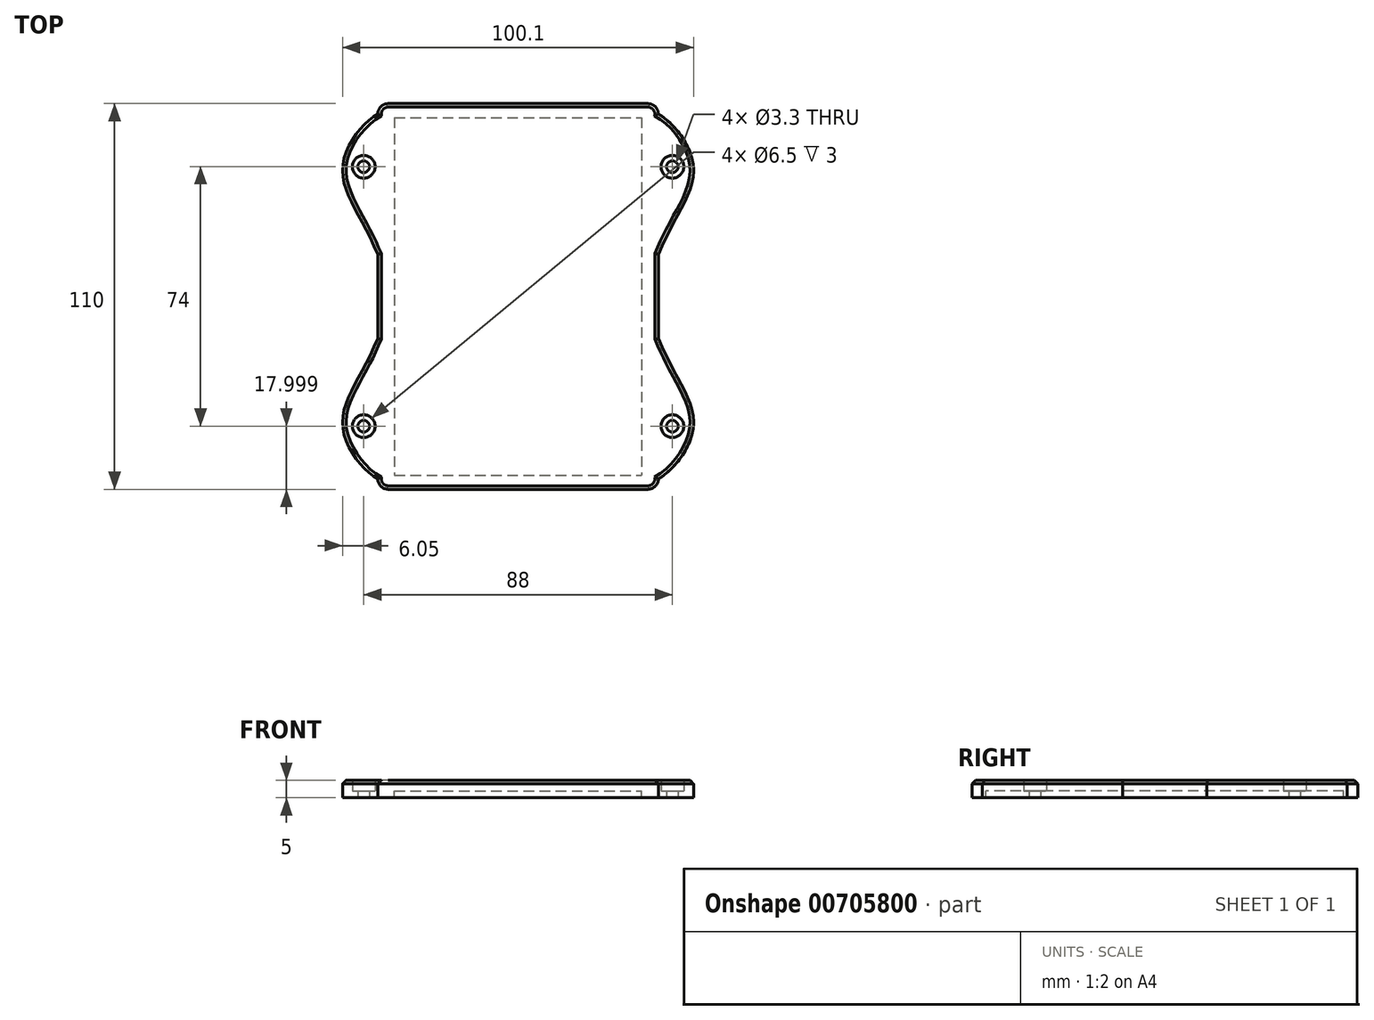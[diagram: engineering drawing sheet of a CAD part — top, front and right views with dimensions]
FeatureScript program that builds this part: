
annotation { "Feature Type Name" : "Feature", "Feature Type Description" : "" }
export const myFeature = defineFeature(function(context is Context, id is Id, definition is map)
    precondition{}
    {
        {
            var Q0;
            Q0=qCreatedBy(makeId("Top.planeOp"),FACE);
            var sketch = newSketch(context, id + "F0", { "sketchPlane" : qUnion([Q0])});
            skLineSegment(sketch, "E0.bottom", {"start": v(-37, 55.33) * mm, "end": v(37, 55.33) * mm});
            skLineSegment(sketch, "E0.top", {"start": v(-37, -54.67) * mm, "end": v(37, -54.67) * mm});
            skLineSegment(sketch, "E0.left", {"start": v(-40, 52.33) * mm, "end": v(-40, -51.67) * mm});
            skLineSegment(sketch, "E0.right", {"start": v(40, 52.33) * mm, "end": v(40, -51.67) * mm});
            skPoint(sketch, "E1.visualSharp", {"position": v(-40, 55.33) * mm});
            skArc(sketch, "E1.filletArc", {"start": v(-37, 55.33) * mm, "mid": v(-39.12, 54.45) * mm, "end": v(-40, 52.33) * mm});
            skPoint(sketch, "E2.visualSharp", {"position": v(40, 55.33) * mm});
            skArc(sketch, "E2.filletArc", {"start": v(40, 52.33) * mm, "mid": v(39.12, 54.45) * mm, "end": v(37, 55.33) * mm});
            skPoint(sketch, "E3.visualSharp", {"position": v(-40, -54.67) * mm});
            skArc(sketch, "E3.filletArc", {"start": v(-40, -51.67) * mm, "mid": v(-39.12, -53.8) * mm, "end": v(-37, -54.67) * mm});
            skPoint(sketch, "E4.visualSharp", {"position": v(40, -54.67) * mm});
            skArc(sketch, "E4.filletArc", {"start": v(37, -54.67) * mm, "mid": v(39.12, -53.8) * mm, "end": v(40, -51.67) * mm});
            skLineSegment(sketch, "E5.bottom", {"start": v(-35.25, 51.33) * mm, "end": v(35.25, 51.33) * mm});
            skLineSegment(sketch, "E5.top", {"start": v(-35.25, -50.67) * mm, "end": v(35.25, -50.67) * mm});
            skLineSegment(sketch, "E5.left", {"start": v(-35.25, 51.33) * mm, "end": v(-35.25, -50.67) * mm});
            skLineSegment(sketch, "E5.right", {"start": v(35.25, 51.33) * mm, "end": v(35.25, -50.67) * mm});
            skPoint(sketch, "E6", {"position": v(-30.86, 36.33) * mm});
            skPoint(sketch, "E7.MirrorP", {"position": v(30.86, 36.33) * mm});
            skPoint(sketch, "E8", {"position": v(-30.86, -40.27) * mm});
            skPoint(sketch, "E9.MirrorP", {"position": v(30.86, -40.27) * mm});
            skFitSpline(sketch, "E10", {"points": [v(40, 52.33) * mm, v(50, 37.33) * mm, v(40, 12.33) * mm], "startDerivative": vector(28.09, -14.91) * mm, "endDerivative": vector(-23.57, -58.35) * mm});
            skFitSpline(sketch, "E11.MirrorCS", {"points": [v(-40, 52.33) * mm, v(-50, 37.33) * mm, v(-40, 12.33) * mm], "startDerivative": vector(-28.09, -14.91) * mm, "endDerivative": vector(23.57, -58.35) * mm});
            skFitSpline(sketch, "E12.MirrorCS", {"points": [v(-40, -51.67) * mm, v(-50, -36.67) * mm, v(-40, -11.67) * mm], "startDerivative": vector(-28.09, 14.91) * mm, "endDerivative": vector(23.57, 58.35) * mm});
            skFitSpline(sketch, "E13.MirrorCS", {"points": [v(40, -51.67) * mm, v(50, -36.67) * mm, v(40, -11.67) * mm], "startDerivative": vector(28.09, 14.91) * mm, "endDerivative": vector(-23.57, 58.35) * mm});
            skPoint(sketch, "E14", {"position": v(-44, 37.33) * mm});
            skPoint(sketch, "E15.MirrorP", {"position": v(44, 37.33) * mm});
            skPoint(sketch, "E16.MirrorP", {"position": v(-44, -36.67) * mm});
            skPoint(sketch, "E17.MirrorP", {"position": v(44, -36.67) * mm});
            skSolve(sketch);
        }
        {
            var Q0;
            Q0=qSketchRegion(id+"F0",true);
            extrude(context, id + "F1", {"entities" : qUnion([Q0]), "oppositeDirection" : true, "depth" : 5 * mm, "offsetDistance" : 25 * mm});
        }
        {
            var Q0;
            Q0=sQuery(id+"F0.wireOp",VERTEX,"E14");
            var Q1;
            Q1=sQuery(id+"F0.wireOp",VERTEX,"E15.MirrorP");
            var Q2;
            Q2=sQuery(id+"F0.wireOp",VERTEX,"E17.MirrorP");
            var Q3;
            Q3=sQuery(id+"F0.wireOp",VERTEX,"E16.MirrorP");
            var Q4;
            Q4=makeQuery(id+"F1.opExtrude","SWEPT_BODY",BODY,{"disambiguationData":[OSD([sQuery(id+"F0.wireOp",EDGE,"E0.bottom"),sQuery(id+"F0.wireOp",EDGE,"E0.top"),sQuery(id+"F0.wireOp",EDGE,"E0.left"),sQuery(id+"F0.wireOp",EDGE,"E0.right"),sQuery(id+"F0.wireOp",EDGE,"E1.filletArc"),sQuery(id+"F0.wireOp",EDGE,"E2.filletArc"),sQuery(id+"F0.wireOp",EDGE,"E3.filletArc"),sQuery(id+"F0.wireOp",EDGE,"E4.filletArc"),sQuery(id+"F0.wireOp",EDGE,"E10"),sQuery(id+"F0.wireOp",EDGE,"E11.MirrorCS"),sQuery(id+"F0.wireOp",EDGE,"E12.MirrorCS"),sQuery(id+"F0.wireOp",EDGE,"E13.MirrorCS")])]});
            hole(context, id + "F2", {"style" : HoleStyle.C_BORE, "endStyle" : HoleEndStyle.THROUGH, "standardTappedOrClearance" : lookupTablePath({ "standard" : "ISO", "fit" : "Normal", "size" : "M3", "type" : "Clearance" }), "standardBlindInLast" : lookupTablePath({ "fit" : "Standard", "standard" : "ISO", "size" : "M3", "type" : "Clearance" }), "holeDiameter" : 3.3 * mm, "cBoreDiameter" : 6.5 * mm, "cBoreDepth" : 3 * mm, "majorDiameter" : 5 * mm, "isTappedThrough" : true, "tappedDepth" : 12 * mm, "tapClearance" : 3, "startFromSketch" : true, "locations" : qUnion([Q0, Q1, Q2, Q3]), "scope" : qUnion([Q4])});
        }
        {
            var Q0;
            Q0=makeQuery(id+"F0.imprint","IMPRINT",FACE,{"disambiguationData":[TD([[makeQuery(id+"F0.imprint","IMPRINT",EDGE,{"derivedFrom":sQuery(id+"F0.wireOp",EDGE,"E5.bottom")}),-1.0]])]});
            extrude(context, id + "F3", {"entities" : qUnion([Q0]), "operationType" : NewBodyOperationType.ADD, "oppositeDirection" : true, "depth" : 3 * mm, "offsetDistance" : 25 * mm});
        }
        {
            var Q0;
            Q0=makeQuery(id+"F1.opExtrude","CAP_EDGE",EDGE,{"disambiguationData":[OSD([sQuery(id+"F0.wireOp",EDGE,"E0.bottom")])],"isStart":true});
            var Q1;
            Q1=makeQuery(id+"F1.opExtrude","CAP_EDGE",EDGE,{"disambiguationData":[OSD([sQuery(id+"F0.wireOp",EDGE,"E11.MirrorCS")])],"isStart":true});
            var Q2;
            Q2=makeQuery(id+"F1.opExtrude","CAP_EDGE",EDGE,{"disambiguationData":[OSD([sQuery(id+"F0.wireOp",EDGE,"E0.left")])],"isStart":true});
            var Q3;
            Q3=makeQuery(id+"F1.opExtrude","CAP_EDGE",EDGE,{"disambiguationData":[OSD([sQuery(id+"F0.wireOp",EDGE,"E12.MirrorCS")])],"isStart":true});
            var Q4;
            Q4=makeQuery(id+"F1.opExtrude","CAP_EDGE",EDGE,{"disambiguationData":[OSD([sQuery(id+"F0.wireOp",EDGE,"E3.filletArc")])],"isStart":true});
            var Q5;
            Q5=makeQuery(id+"F1.opExtrude","CAP_EDGE",EDGE,{"disambiguationData":[OSD([sQuery(id+"F0.wireOp",EDGE,"E13.MirrorCS")])],"isStart":true});
            var Q6;
            Q6=makeQuery(id+"F1.opExtrude","CAP_EDGE",EDGE,{"disambiguationData":[OSD([sQuery(id+"F0.wireOp",EDGE,"E0.top")])],"isStart":true});
            var Q7;
            Q7=makeQuery(id+"F1.opExtrude","CAP_EDGE",EDGE,{"disambiguationData":[OSD([sQuery(id+"F0.wireOp",EDGE,"E4.filletArc")])],"isStart":true});
            var Q8;
            Q8=makeQuery(id+"F1.opExtrude","CAP_EDGE",EDGE,{"disambiguationData":[OSD([sQuery(id+"F0.wireOp",EDGE,"E0.right")])],"isStart":true});
            var Q9;
            Q9=makeQuery(id+"F1.opExtrude","CAP_EDGE",EDGE,{"disambiguationData":[OSD([sQuery(id+"F0.wireOp",EDGE,"E10")])],"isStart":true});
            var Q10;
            Q10=makeQuery(id+"F1.opExtrude","CAP_EDGE",EDGE,{"disambiguationData":[OSD([sQuery(id+"F0.wireOp",EDGE,"E2.filletArc")])],"isStart":true});
            var Q11;
            Q11=makeQuery(id+"F1.opExtrude","CAP_EDGE",EDGE,{"disambiguationData":[OSD([sQuery(id+"F0.wireOp",EDGE,"E1.filletArc")])],"isStart":true});
            var Q12;
            {var subQ0=sQuery(id+"F0.wireOp",EDGE,"E5.right");var subQ1=sQuery(id+"F0.wireOp",EDGE,"E5.left");var subQ2=sQuery(id+"F0.wireOp",EDGE,"E5.top");var subQ3=sQuery(id+"F0.wireOp",EDGE,"E5.bottom");Q12=makeQuery(id+"Ft1h9bfuAKPQ5jx_1.boolean.opBoolean","INTERSECT",EDGE,{"derivedFrom":[makeQuery(id+"F3.boolean.opBoolean","MERGE",FACE,{"derivedFrom":[makeQuery(id+"F1.opExtrude","CAP_FACE",FACE,{"disambiguationData":[OSD([sQuery(id+"F0.wireOp",EDGE,"E0.bottom"),sQuery(id+"F0.wireOp",EDGE,"E0.top"),sQuery(id+"F0.wireOp",EDGE,"E0.left"),sQuery(id+"F0.wireOp",EDGE,"E0.right"),sQuery(id+"F0.wireOp",EDGE,"E1.filletArc"),sQuery(id+"F0.wireOp",EDGE,"E2.filletArc"),sQuery(id+"F0.wireOp",EDGE,"E3.filletArc"),sQuery(id+"F0.wireOp",EDGE,"E4.filletArc"),subQ3,subQ2,subQ1,subQ0,sQuery(id+"F0.wireOp",EDGE,"E10"),sQuery(id+"F0.wireOp",EDGE,"E11.MirrorCS"),sQuery(id+"F0.wireOp",EDGE,"E12.MirrorCS"),sQuery(id+"F0.wireOp",EDGE,"E13.MirrorCS")])],"isStart":true}),makeQuery(id+"F3.opExtrude","CAP_FACE",FACE,{"disambiguationData":[OSD([subQ3,subQ2,subQ1,subQ0])],"isStart":true})]}),makeQuery(id+"Ft1h9bfuAKPQ5jx_1.opExtrude","SWEPT_FACE",FACE,{"disambiguationData":[OSD([sQuery(id+"FdBzHQuVNLFFk73_1.wireOp",EDGE,"U0Z58mjc-AaiX-j66n-ui4p-18zjtXrbp7Po")])]})]});}
            chamfer(context, id + "F4", {"entities" : qUnion([Q0, Q1, Q2, Q3, Q4, Q5, Q6, Q7, Q8, Q9, Q10, Q11, Q12]), "width" : 1 * mm, "tangentPropagation" : true});
        }
    });
